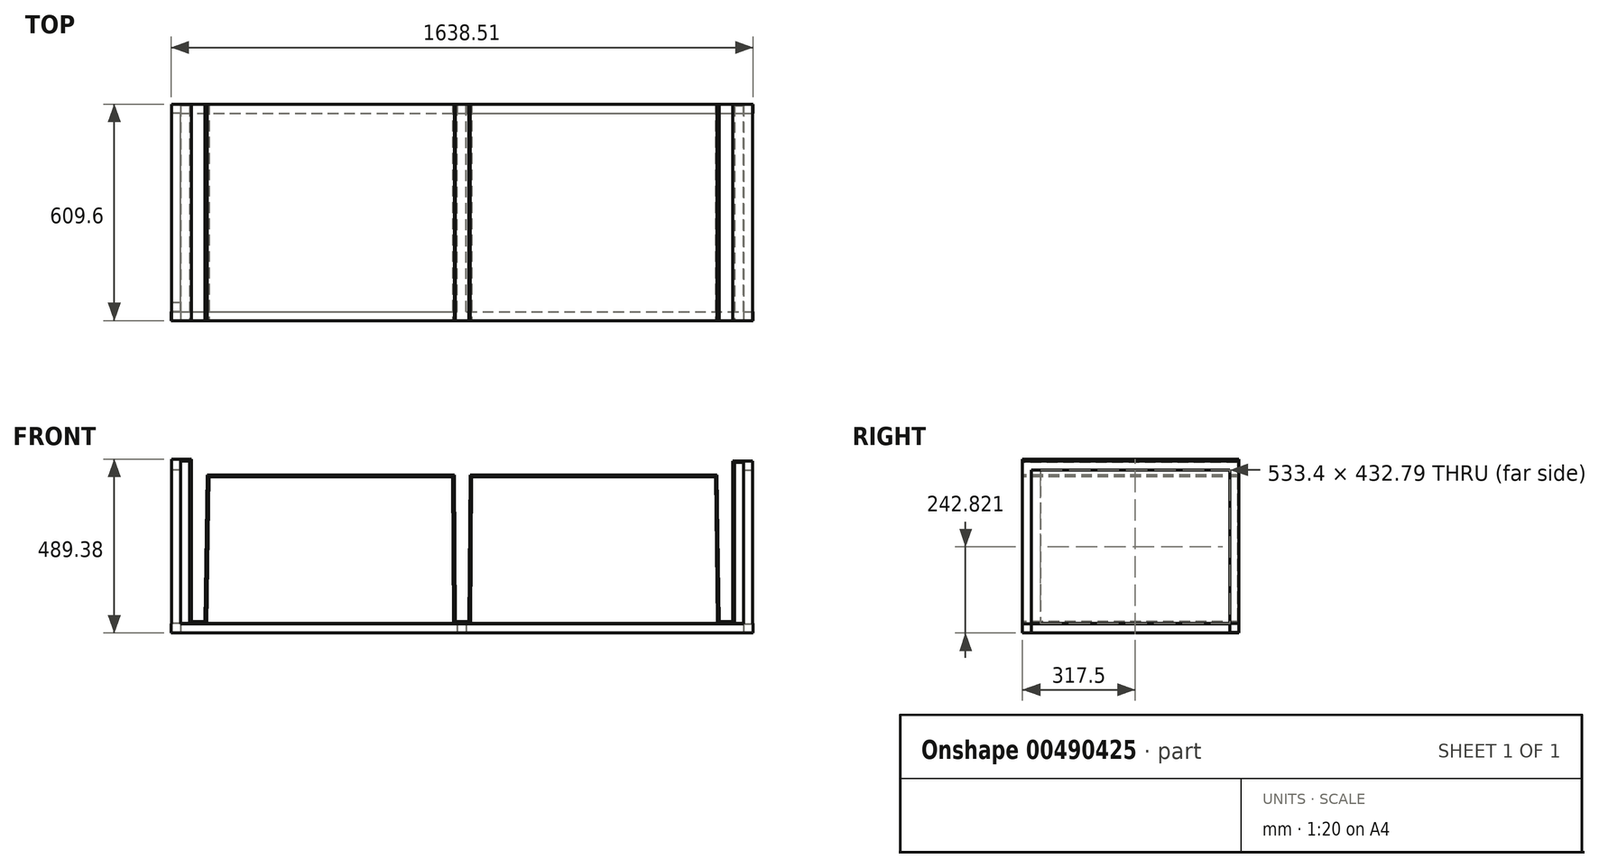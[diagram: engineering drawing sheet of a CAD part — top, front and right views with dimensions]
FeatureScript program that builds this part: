
annotation { "Feature Type Name" : "Feature", "Feature Type Description" : "" }
export const myFeature = defineFeature(function(context is Context, id is Id, definition is map)
    precondition{}
    {
        {
            var Q0;
            Q0=qCreatedBy(makeId("Front.planeOp"),FACE);
            var sketch = newSketch(context, id + "F0", { "sketchPlane" : qUnion([Q0])});
            skLineSegment(sketch, "E0", {"start": v(-453.27, -261.56) * mm, "end": v(-453.27, 195.64) * mm});
            skLineSegment(sketch, "E1", {"start": v(-453.27, -261.56) * mm, "end": v(-415.17, -261.56) * mm});
            skLineSegment(sketch, "E2", {"start": v(1070.73, 190.88) * mm, "end": v(1070.73, -261.56) * mm});
            skPoint(sketch, "E2.endSnap0", {"position": v(-434.22, -261.56) * mm});
            skLineSegment(sketch, "E3", {"start": v(-408.82, 151.19) * mm, "end": v(-415.17, -261.56) * mm});
            skLineSegment(sketch, "E4", {"start": v(1070.73, -261.56) * mm, "end": v(1032.63, -261.56) * mm});
            skLineSegment(sketch, "E5", {"start": v(1026.28, 151.19) * mm, "end": v(1032.63, -261.56) * mm});
            skLineSegment(sketch, "E6", {"start": v(-408.82, 151.19) * mm, "end": v(286.5, 151.19) * mm});
            skLineSegment(sketch, "E7", {"start": v(1026.28, 151.19) * mm, "end": v(330.96, 151.19) * mm});
            skLineSegment(sketch, "E8", {"start": v(327.78, -261.56) * mm, "end": v(330.96, 151.19) * mm});
            skLineSegment(sketch, "E9", {"start": v(327.78, -261.56) * mm, "end": v(289.68, -261.56) * mm});
            skLineSegment(sketch, "E10", {"start": v(289.68, -261.56) * mm, "end": v(286.5, 151.19) * mm});
            skLineSegment(sketch, "E11", {"start": v(-453.27, 195.64) * mm, "end": v(-458.03, 195.64) * mm});
            skLineSegment(sketch, "E12", {"start": v(-458.03, 195.64) * mm, "end": v(-458.03, -261.56) * mm});
            skLineSegment(sketch, "E13", {"start": v(-458.03, -261.56) * mm, "end": v(-453.27, -261.56) * mm});
            skLineSegment(sketch, "E14", {"start": v(-458.03, -261.56) * mm, "end": v(-458.03, -266.32) * mm});
            skLineSegment(sketch, "E15", {"start": v(-458.03, -266.32) * mm, "end": v(-415.17, -266.98) * mm});
            skLineSegment(sketch, "E16", {"start": v(-415.17, -266.98) * mm, "end": v(-415.17, -261.56) * mm});
            skLineSegment(sketch, "E17", {"start": v(-415.17, -266.98) * mm, "end": v(-410.4, -266.98) * mm});
            skLineSegment(sketch, "E18", {"start": v(-410.4, -266.98) * mm, "end": v(-403.97, 151.19) * mm});
            skLineSegment(sketch, "E19", {"start": v(-408.82, 151.19) * mm, "end": v(-408.82, 146.43) * mm});
            skLineSegment(sketch, "E20", {"start": v(-408.82, 146.43) * mm, "end": v(286.54, 146.43) * mm});
            skLineSegment(sketch, "E21", {"start": v(289.68, -261.56) * mm, "end": v(284.92, -261.56) * mm});
            skLineSegment(sketch, "E22", {"start": v(284.92, -261.56) * mm, "end": v(281.78, 146.43) * mm});
            skLineSegment(sketch, "E23", {"start": v(284.92, -261.56) * mm, "end": v(284.92, -266.32) * mm});
            skLineSegment(sketch, "E24", {"start": v(284.92, -266.32) * mm, "end": v(327.78, -266.32) * mm});
            skLineSegment(sketch, "E25", {"start": v(327.78, -266.32) * mm, "end": v(327.78, -261.56) * mm});
            skLineSegment(sketch, "E26", {"start": v(327.78, -266.32) * mm, "end": v(332.55, -266.36) * mm});
            skLineSegment(sketch, "E27", {"start": v(332.55, -266.36) * mm, "end": v(335.76, 151.19) * mm});
            skLineSegment(sketch, "E28", {"start": v(330.96, 151.19) * mm, "end": v(330.96, 146.43) * mm});
            skLineSegment(sketch, "E29", {"start": v(330.96, 146.43) * mm, "end": v(1026.36, 146.43) * mm});
            skLineSegment(sketch, "E30", {"start": v(1026.28, 151.19) * mm, "end": v(1021.52, 151.19) * mm});
            skLineSegment(sketch, "E31", {"start": v(1021.52, 151.19) * mm, "end": v(1027.87, -261.56) * mm});
            skLineSegment(sketch, "E32", {"start": v(1027.87, -261.56) * mm, "end": v(1032.63, -261.56) * mm});
            skLineSegment(sketch, "E33", {"start": v(1027.87, -261.56) * mm, "end": v(1027.87, -266.32) * mm});
            skLineSegment(sketch, "E34", {"start": v(1027.87, -266.32) * mm, "end": v(1070.73, -266.32) * mm});
            skLineSegment(sketch, "E35", {"start": v(1070.73, -266.32) * mm, "end": v(1070.73, -261.56) * mm});
            skLineSegment(sketch, "E36", {"start": v(1070.73, -266.32) * mm, "end": v(1075.5, -266.32) * mm});
            skLineSegment(sketch, "E37", {"start": v(1075.5, -266.32) * mm, "end": v(1075.5, 190.88) * mm});
            skLineSegment(sketch, "E38", {"start": v(1075.5, 190.88) * mm, "end": v(1070.73, 190.88) * mm});
            skSolve(sketch);
        }
        {
            var Q0;
            Q0 = qSketchRegion(id + "F0", true);
            extrude(context, id + "F1", {"entities" : qUnion([Q0]), "depth" : -609.6 * mm});
        }
        {
            var Q0;
            Q0=makeQuery(id+"F1.opExtrude","CAP_FACE",FACE,{"disambiguationData":[OSD([sQuery(id+"F0.wireOp",EDGE,"E0"),sQuery(id+"F0.wireOp",EDGE,"E1"),sQuery(id+"F0.wireOp",EDGE,"E2"),sQuery(id+"F0.wireOp",EDGE,"E3"),sQuery(id+"F0.wireOp",EDGE,"E4"),sQuery(id+"F0.wireOp",EDGE,"E5"),sQuery(id+"F0.wireOp",EDGE,"E6"),sQuery(id+"F0.wireOp",EDGE,"E7"),sQuery(id+"F0.wireOp",EDGE,"E8"),sQuery(id+"F0.wireOp",EDGE,"E9"),sQuery(id+"F0.wireOp",EDGE,"E10"),sQuery(id+"F0.wireOp",EDGE,"E11"),sQuery(id+"F0.wireOp",EDGE,"E12"),sQuery(id+"F0.wireOp",EDGE,"E14"),sQuery(id+"F0.wireOp",EDGE,"E15"),sQuery(id+"F0.wireOp",EDGE,"E17"),sQuery(id+"F0.wireOp",EDGE,"E18"),sQuery(id+"F0.wireOp",EDGE,"E20"),sQuery(id+"F0.wireOp",EDGE,"E22"),sQuery(id+"F0.wireOp",EDGE,"E23"),sQuery(id+"F0.wireOp",EDGE,"E24"),sQuery(id+"F0.wireOp",EDGE,"E26"),sQuery(id+"F0.wireOp",EDGE,"E27"),sQuery(id+"F0.wireOp",EDGE,"E29"),sQuery(id+"F0.wireOp",EDGE,"E30"),sQuery(id+"F0.wireOp",EDGE,"E31"),sQuery(id+"F0.wireOp",EDGE,"E33"),sQuery(id+"F0.wireOp",EDGE,"E34"),sQuery(id+"F0.wireOp",EDGE,"E36"),sQuery(id+"F0.wireOp",EDGE,"E37"),sQuery(id+"F0.wireOp",EDGE,"E38")])],"isStart":true});
            var sketch = newSketch(context, id + "F2", { "sketchPlane" : qUnion([Q0])});
            skLineSegment(sketch, "E39.bottom", {"start": v(-458.03, 195.64) * mm, "end": v(-508.83, 195.64) * mm});
            skLineSegment(sketch, "E39.top", {"start": v(-458.03, 190.88) * mm, "end": v(-508.83, 190.88) * mm});
            skLineSegment(sketch, "E39.left", {"start": v(-458.03, 195.64) * mm, "end": v(-458.03, 190.88) * mm});
            skLineSegment(sketch, "E39.right", {"start": v(-508.83, 195.64) * mm, "end": v(-508.83, 190.88) * mm});
            skLineSegment(sketch, "E40.bottom", {"start": v(1075.5, 190.88) * mm, "end": v(1126.3, 190.88) * mm});
            skLineSegment(sketch, "E40.top", {"start": v(1075.5, 186.11) * mm, "end": v(1126.3, 186.11) * mm});
            skLineSegment(sketch, "E40.left", {"start": v(1075.5, 190.88) * mm, "end": v(1075.5, 186.11) * mm});
            skLineSegment(sketch, "E40.right", {"start": v(1126.3, 190.88) * mm, "end": v(1126.3, 186.11) * mm});
            skSolve(sketch);
        }
        {
            var Q0;
            Q0=makeQuery(id+"F2.imprint","IMPRINT",FACE,{"disambiguationData":[TD([[makeQuery(id+"F2.imprint","IMPRINT",EDGE,{"derivedFrom":sQuery(id+"F2.wireOp",EDGE,"E39.bottom")}),1.0]])]});
            extrude(context, id + "F3", {"entities" : qUnion([Q0]), "operationType" : NewBodyOperationType.ADD, "depth" : -609.6 * mm});
        }
        {
            var Q0;
            Q0 = qSketchRegion(id + "F2", true);
            extrude(context, id + "F4", {"entities" : qUnion([Q0]), "operationType" : NewBodyOperationType.ADD, "depth" : -609.6 * mm});
        }
        {
            var Q0;
            Q0=makeQuery(id+"F4.boolean.opBoolean","MERGE",FACE,{"derivedFrom":[makeQuery(id+"F3.boolean.opBoolean","MERGE",FACE,{"derivedFrom":[makeQuery(id+"F1.opExtrude","CAP_FACE",FACE,{"disambiguationData":[OSD([sQuery(id+"F0.wireOp",EDGE,"E0"),sQuery(id+"F0.wireOp",EDGE,"E1"),sQuery(id+"F0.wireOp",EDGE,"E2"),sQuery(id+"F0.wireOp",EDGE,"E3"),sQuery(id+"F0.wireOp",EDGE,"E4"),sQuery(id+"F0.wireOp",EDGE,"E5"),sQuery(id+"F0.wireOp",EDGE,"E6"),sQuery(id+"F0.wireOp",EDGE,"E7"),sQuery(id+"F0.wireOp",EDGE,"E8"),sQuery(id+"F0.wireOp",EDGE,"E9"),sQuery(id+"F0.wireOp",EDGE,"E10"),sQuery(id+"F0.wireOp",EDGE,"E11"),sQuery(id+"F0.wireOp",EDGE,"E12"),sQuery(id+"F0.wireOp",EDGE,"E14"),sQuery(id+"F0.wireOp",EDGE,"E15"),sQuery(id+"F0.wireOp",EDGE,"E17"),sQuery(id+"F0.wireOp",EDGE,"E18"),sQuery(id+"F0.wireOp",EDGE,"E20"),sQuery(id+"F0.wireOp",EDGE,"E22"),sQuery(id+"F0.wireOp",EDGE,"E23"),sQuery(id+"F0.wireOp",EDGE,"E24"),sQuery(id+"F0.wireOp",EDGE,"E26"),sQuery(id+"F0.wireOp",EDGE,"E27"),sQuery(id+"F0.wireOp",EDGE,"E29"),sQuery(id+"F0.wireOp",EDGE,"E30"),sQuery(id+"F0.wireOp",EDGE,"E31"),sQuery(id+"F0.wireOp",EDGE,"E33"),sQuery(id+"F0.wireOp",EDGE,"E34"),sQuery(id+"F0.wireOp",EDGE,"E36"),sQuery(id+"F0.wireOp",EDGE,"E37"),sQuery(id+"F0.wireOp",EDGE,"E38")])],"isStart":true}),makeQuery(id+"F3.opExtrude","CAP_FACE",FACE,{"disambiguationData":[OSD([sQuery(id+"F2.wireOp",EDGE,"E39.bottom"),sQuery(id+"F2.wireOp",EDGE,"E39.top"),sQuery(id+"F2.wireOp",EDGE,"E39.left"),sQuery(id+"F2.wireOp",EDGE,"E39.right")])],"isStart":true})]}),makeQuery(id+"F4.opExtrude","CAP_FACE",FACE,{"disambiguationData":[OSD([sQuery(id+"F2.wireOp",EDGE,"E40.bottom"),sQuery(id+"F2.wireOp",EDGE,"E40.top"),sQuery(id+"F2.wireOp",EDGE,"E40.left"),sQuery(id+"F2.wireOp",EDGE,"E40.right")])],"isStart":true})]});
            var sketch = newSketch(context, id + "F5", { "sketchPlane" : qUnion([Q0])});
            skLineSegment(sketch, "E41.bottom", {"start": v(-508.83, 190.88) * mm, "end": v(-483.43, 190.88) * mm});
            skLineSegment(sketch, "E41.top", {"start": v(-508.83, -271.09) * mm, "end": v(-483.43, -271.09) * mm});
            skLineSegment(sketch, "E41.left", {"start": v(-508.83, 190.88) * mm, "end": v(-508.83, -271.09) * mm});
            skLineSegment(sketch, "E41.right", {"start": v(-483.43, 190.88) * mm, "end": v(-483.43, -271.09) * mm});
            skLineSegment(sketch, "E42.bottom", {"start": v(1126.3, 186.11) * mm, "end": v(1100.9, 186.11) * mm});
            skLineSegment(sketch, "E42.top", {"start": v(1126.3, -275.85) * mm, "end": v(1100.9, -275.85) * mm});
            skLineSegment(sketch, "E42.left", {"start": v(1126.3, 186.11) * mm, "end": v(1126.3, -275.85) * mm});
            skLineSegment(sketch, "E42.right", {"start": v(1100.9, 186.11) * mm, "end": v(1100.9, -275.85) * mm});
            skSolve(sketch);
        }
        {
            var Q0;
            Q0 = qSketchRegion(id + "F5", true);
            extrude(context, id + "F6", {"entities" : qUnion([Q0]), "operationType" : NewBodyOperationType.ADD, "depth" : -25.4 * mm});
        }
        {
            var Q0;
            Q0=makeQuery(id+"F6.boolean.opBoolean","MERGE",FACE,{"derivedFrom":[makeQuery(id+"F4.boolean.opBoolean","MERGE",FACE,{"derivedFrom":[makeQuery(id+"F3.boolean.opBoolean","MERGE",FACE,{"derivedFrom":[makeQuery(id+"F1.opExtrude","CAP_FACE",FACE,{"disambiguationData":[OSD([sQuery(id+"F0.wireOp",EDGE,"E0"),sQuery(id+"F0.wireOp",EDGE,"E1"),sQuery(id+"F0.wireOp",EDGE,"E2"),sQuery(id+"F0.wireOp",EDGE,"E3"),sQuery(id+"F0.wireOp",EDGE,"E4"),sQuery(id+"F0.wireOp",EDGE,"E5"),sQuery(id+"F0.wireOp",EDGE,"E6"),sQuery(id+"F0.wireOp",EDGE,"E7"),sQuery(id+"F0.wireOp",EDGE,"E8"),sQuery(id+"F0.wireOp",EDGE,"E9"),sQuery(id+"F0.wireOp",EDGE,"E10"),sQuery(id+"F0.wireOp",EDGE,"E11"),sQuery(id+"F0.wireOp",EDGE,"E12"),sQuery(id+"F0.wireOp",EDGE,"E14"),sQuery(id+"F0.wireOp",EDGE,"E15"),sQuery(id+"F0.wireOp",EDGE,"E17"),sQuery(id+"F0.wireOp",EDGE,"E18"),sQuery(id+"F0.wireOp",EDGE,"E20"),sQuery(id+"F0.wireOp",EDGE,"E22"),sQuery(id+"F0.wireOp",EDGE,"E23"),sQuery(id+"F0.wireOp",EDGE,"E24"),sQuery(id+"F0.wireOp",EDGE,"E26"),sQuery(id+"F0.wireOp",EDGE,"E27"),sQuery(id+"F0.wireOp",EDGE,"E29"),sQuery(id+"F0.wireOp",EDGE,"E30"),sQuery(id+"F0.wireOp",EDGE,"E31"),sQuery(id+"F0.wireOp",EDGE,"E33"),sQuery(id+"F0.wireOp",EDGE,"E34"),sQuery(id+"F0.wireOp",EDGE,"E36"),sQuery(id+"F0.wireOp",EDGE,"E37"),sQuery(id+"F0.wireOp",EDGE,"E38")])],"isStart":true}),makeQuery(id+"F3.opExtrude","CAP_FACE",FACE,{"disambiguationData":[OSD([sQuery(id+"F2.wireOp",EDGE,"E39.bottom"),sQuery(id+"F2.wireOp",EDGE,"E39.top"),sQuery(id+"F2.wireOp",EDGE,"E39.left"),sQuery(id+"F2.wireOp",EDGE,"E39.right")])],"isStart":true})]}),makeQuery(id+"F4.opExtrude","CAP_FACE",FACE,{"disambiguationData":[OSD([sQuery(id+"F2.wireOp",EDGE,"E40.bottom"),sQuery(id+"F2.wireOp",EDGE,"E40.top"),sQuery(id+"F2.wireOp",EDGE,"E40.left"),sQuery(id+"F2.wireOp",EDGE,"E40.right")])],"isStart":true})]}),makeQuery(id+"F6.opExtrude","CAP_FACE",FACE,{"disambiguationData":[OSD([sQuery(id+"F5.wireOp",EDGE,"PXd4t3fK-VJNK-RpV8-3AYd-AQfVrzeM2m9b.bottom"),sQuery(id+"F5.wireOp",EDGE,"PXd4t3fK-VJNK-RpV8-3AYd-AQfVrzeM2m9b.top"),sQuery(id+"F5.wireOp",EDGE,"PXd4t3fK-VJNK-RpV8-3AYd-AQfVrzeM2m9b.left"),sQuery(id+"F5.wireOp",EDGE,"PXd4t3fK-VJNK-RpV8-3AYd-AQfVrzeM2m9b.right")])],"isStart":true}),makeQuery(id+"F6.opExtrude","CAP_FACE",FACE,{"disambiguationData":[OSD([sQuery(id+"F5.wireOp",EDGE,"UQCXd49x-7FcS-RsmS-loZU-28u0bhkUhXdd.bottom"),sQuery(id+"F5.wireOp",EDGE,"UQCXd49x-7FcS-RsmS-loZU-28u0bhkUhXdd.top"),sQuery(id+"F5.wireOp",EDGE,"UQCXd49x-7FcS-RsmS-loZU-28u0bhkUhXdd.left"),sQuery(id+"F5.wireOp",EDGE,"UQCXd49x-7FcS-RsmS-loZU-28u0bhkUhXdd.right")])],"isStart":true})]});
            var sketch = newSketch(context, id + "F7", { "sketchPlane" : qUnion([Q0])});
            skSolve(sketch);
        }
        {
            var Q0;
            Q0 = qSketchRegion(id + "F5", true);
            extrude(context, id + "F8", {"entities" : qUnion([Q0]), "operationType" : NewBodyOperationType.ADD, "depth" : -25.4 * mm});
        }
        {
            var Q0;
            Q0=makeQuery(id+"F7.imprint","IMPRINT",FACE,{"disambiguationData":[TD([[makeQuery(id+"F7.imprint","IMPRINT",EDGE,{"derivedFrom":makeQuery(id+"F1.opExtrude","CAP_EDGE",EDGE,{"disambiguationData":[OSD([sQuery(id+"F0.wireOp",EDGE,"E0")])],"isStart":true})}),1.0]])]});
            var sketch = newSketch(context, id + "F9", { "sketchPlane" : qUnion([Q0])});
            skLineSegment(sketch, "E43.bottom", {"start": v(-510.8, -268.34) * mm, "end": v(1127.1, -268.34) * mm});
            skLineSegment(sketch, "E43.top", {"start": v(-510.8, -293.74) * mm, "end": v(1127.1, -293.74) * mm});
            skLineSegment(sketch, "E43.left", {"start": v(-510.8, -268.34) * mm, "end": v(-510.8, -293.74) * mm});
            skLineSegment(sketch, "E43.right", {"start": v(1127.1, -268.34) * mm, "end": v(1127.1, -293.74) * mm});
            skSolve(sketch);
        }
        {
            var Q0;
            Q0 = qSketchRegion(id + "F9", true);
            extrude(context, id + "F10", {"entities" : qUnion([Q0]), "operationType" : NewBodyOperationType.ADD, "depth" : -25.4 * mm});
        }
        {
            var Q0;
            Q0=makeQuery(id+"F6.boolean.opBoolean","MERGE",FACE,{"derivedFrom":[makeQuery(id+"F4.opExtrude","SWEPT_FACE",FACE,{"disambiguationData":[OSD([sQuery(id+"F2.wireOp",EDGE,"E40.right")])]}),makeQuery(id+"F6.opExtrude","SWEPT_FACE",FACE,{"disambiguationData":[OSD([sQuery(id+"F5.wireOp",EDGE,"E42.left")])]})]});
            var sketch = newSketch(context, id + "F11", { "sketchPlane" : qUnion([Q0])});
            skLineSegment(sketch, "E44.bottom", {"start": v(0, 190.88) * mm, "end": v(609.6, 190.88) * mm});
            skLineSegment(sketch, "E44.top", {"start": v(0, 165.48) * mm, "end": v(609.6, 165.48) * mm});
            skLineSegment(sketch, "E44.left", {"start": v(0, 190.88) * mm, "end": v(0, 165.48) * mm});
            skLineSegment(sketch, "E44.right", {"start": v(609.6, 190.88) * mm, "end": v(609.6, 165.48) * mm});
            skLineSegment(sketch, "E45.bottom", {"start": v(609.6, 165.48) * mm, "end": v(584.2, 165.48) * mm});
            skLineSegment(sketch, "E46.bottom", {"start": v(25.4, -268.34) * mm, "end": v(609.6, -268.34) * mm});
            skLineSegment(sketch, "E46.top", {"start": v(25.4, -293.74) * mm, "end": v(609.6, -293.74) * mm});
            skLineSegment(sketch, "E46.left", {"start": v(25.4, -268.34) * mm, "end": v(25.4, -293.74) * mm});
            skLineSegment(sketch, "E46.right", {"start": v(609.6, -268.34) * mm, "end": v(609.6, -293.74) * mm});
            skLineSegment(sketch, "E47.top", {"start": v(609.6, -268.34) * mm, "end": v(584.2, -268.34) * mm});
            skLineSegment(sketch, "E47.left", {"start": v(609.6, 165.48) * mm, "end": v(609.6, -268.34) * mm});
            skLineSegment(sketch, "E47.right", {"start": v(584.2, 165.48) * mm, "end": v(584.2, -268.34) * mm});
            skSolve(sketch);
        }
        {
            var Q0;
            Q0 = qSketchRegion(id + "F11", true);
            extrude(context, id + "F12", {"entities" : qUnion([Q0]), "operationType" : NewBodyOperationType.ADD, "depth" : -25.4 * mm});
        }
        {
            var Q0;
            Q0 = qSketchRegion(id + "F11", true);
            extrude(context, id + "F13", {"entities" : qUnion([Q0]), "operationType" : NewBodyOperationType.ADD, "depth" : -25.4 * mm});
        }
        {
            var Q0;
            Q0=makeQuery(id+"F6.boolean.opBoolean","MERGE",FACE,{"derivedFrom":[makeQuery(id+"F3.opExtrude","SWEPT_FACE",FACE,{"disambiguationData":[OSD([sQuery(id+"F2.wireOp",EDGE,"E39.right")])]}),makeQuery(id+"F6.opExtrude","SWEPT_FACE",FACE,{"disambiguationData":[OSD([sQuery(id+"F5.wireOp",EDGE,"E41.left")])]})]});
            var sketch = newSketch(context, id + "F14", { "sketchPlane" : qUnion([Q0])});
            skLineSegment(sketch, "E48.bottom", {"start": v(-25.4, 190.88) * mm, "end": v(-609.6, 190.88) * mm});
            skLineSegment(sketch, "E48.top", {"start": v(-25.4, 165.48) * mm, "end": v(-609.6, 165.48) * mm});
            skLineSegment(sketch, "E48.left", {"start": v(-25.4, 190.88) * mm, "end": v(-25.4, 165.48) * mm});
            skLineSegment(sketch, "E48.right", {"start": v(-609.6, 190.88) * mm, "end": v(-609.6, 165.48) * mm});
            skLineSegment(sketch, "E49.bottom", {"start": v(-25.4, 165.48) * mm, "end": v(-50.8, 165.48) * mm});
            skLineSegment(sketch, "E49.top", {"start": v(-25.4, -267.32) * mm, "end": v(-50.8, -267.32) * mm});
            skLineSegment(sketch, "E49.left", {"start": v(-25.4, 165.48) * mm, "end": v(-25.4, -267.32) * mm});
            skLineSegment(sketch, "E49.right", {"start": v(-50.8, 165.48) * mm, "end": v(-50.8, -267.32) * mm});
            skLineSegment(sketch, "E50.bottom", {"start": v(-25.4, -267.32) * mm, "end": v(-609.6, -267.32) * mm});
            skLineSegment(sketch, "E50.top", {"start": v(-25.4, -292.72) * mm, "end": v(-609.6, -292.72) * mm});
            skLineSegment(sketch, "E50.left", {"start": v(-25.4, -267.32) * mm, "end": v(-25.4, -292.72) * mm});
            skLineSegment(sketch, "E50.right", {"start": v(-609.6, -267.32) * mm, "end": v(-609.6, -292.72) * mm});
            skLineSegment(sketch, "E51.bottom", {"start": v(-609.6, 165.48) * mm, "end": v(-584.2, 165.48) * mm});
            skLineSegment(sketch, "E51.top", {"start": v(-609.6, -267.32) * mm, "end": v(-584.2, -267.32) * mm});
            skLineSegment(sketch, "E51.left", {"start": v(-609.6, 165.48) * mm, "end": v(-609.6, -267.32) * mm});
            skLineSegment(sketch, "E51.right", {"start": v(-584.2, 165.48) * mm, "end": v(-584.2, -267.32) * mm});
            skSolve(sketch);
        }
        {
            var Q0;
            Q0 = qSketchRegion(id + "F14", true);
            extrude(context, id + "F15", {"entities" : qUnion([Q0]), "operationType" : NewBodyOperationType.ADD, "depth" : -25.4 * mm});
        }
        {
            var Q0;
            Q0=makeQuery(id+"F15.opExtrude","SWEPT_FACE",FACE,{"disambiguationData":[OSD([sQuery(id+"F14.wireOp",EDGE,"E50.top")])]});
            var sketch = newSketch(context, id + "F16", { "sketchPlane" : qUnion([Q0])});
            skLineSegment(sketch, "E52.bottom", {"start": v(-508.83, -609.6) * mm, "end": v(1127.72, -609.6) * mm});
            skLineSegment(sketch, "E52.top", {"start": v(-508.83, -584.2) * mm, "end": v(1127.72, -584.2) * mm});
            skLineSegment(sketch, "E52.left", {"start": v(-508.83, -609.6) * mm, "end": v(-508.83, -584.2) * mm});
            skLineSegment(sketch, "E52.right", {"start": v(1127.72, -609.6) * mm, "end": v(1127.72, -584.2) * mm});
            skSolve(sketch);
        }
        {
            var Q0;
            Q0 = qSketchRegion(id + "F16", true);
            extrude(context, id + "F17", {"entities" : qUnion([Q0]), "operationType" : NewBodyOperationType.ADD, "depth" : -25.4 * mm});
        }
        {
            var Q0;
            Q0=makeQuery(id+"F12.boolean.opBoolean","MERGE",FACE,{"derivedFrom":[makeQuery(id+"F10.opExtrude","SWEPT_FACE",FACE,{"disambiguationData":[OSD([sQuery(id+"F9.wireOp",EDGE,"E43.top")])]}),makeQuery(id+"F12.opExtrude","SWEPT_FACE",FACE,{"disambiguationData":[OSD([sQuery(id+"F11.wireOp",EDGE,"E46.top")])]})]});
            var sketch = newSketch(context, id + "F18", { "sketchPlane" : qUnion([Q0])});
            skPoint(sketch, "E53.firstSnap0", {"position": v(295.05, -25.4) * mm});
            skLineSegment(sketch, "E53.bottom", {"start": v(295.05, 0) * mm, "end": v(320.45, 0) * mm});
            skLineSegment(sketch, "E53.top", {"start": v(295.05, -609.6) * mm, "end": v(320.45, -609.6) * mm});
            skLineSegment(sketch, "E53.left", {"start": v(295.05, 0) * mm, "end": v(295.05, -609.6) * mm});
            skLineSegment(sketch, "E53.right", {"start": v(320.45, 0) * mm, "end": v(320.45, -609.6) * mm});
            skSolve(sketch);
        }
        {
            var Q0;
            Q0 = qSketchRegion(id + "F18", true);
            extrude(context, id + "F19", {"entities" : qUnion([Q0]), "operationType" : NewBodyOperationType.ADD, "depth" : -25.4 * mm});
        }
        {
            var Q0;
            Q0=makeQuery(id+"F19.boolean.opBoolean","MERGE",FACE,{"derivedFrom":[makeQuery(id+"F17.boolean.opBoolean","MERGE",FACE,{"derivedFrom":[makeQuery(id+"F15.boolean.opBoolean","MERGE",FACE,{"derivedFrom":[makeQuery(id+"F12.boolean.opBoolean","MERGE",FACE,{"derivedFrom":[makeQuery(id+"F4.boolean.opBoolean","MERGE",FACE,{"derivedFrom":[makeQuery(id+"F3.boolean.opBoolean","MERGE",FACE,{"derivedFrom":[makeQuery(id+"F1.opExtrude","CAP_FACE",FACE,{"disambiguationData":[OSD([sQuery(id+"F0.wireOp",EDGE,"E0"),sQuery(id+"F0.wireOp",EDGE,"E1"),sQuery(id+"F0.wireOp",EDGE,"E2"),sQuery(id+"F0.wireOp",EDGE,"E3"),sQuery(id+"F0.wireOp",EDGE,"E4"),sQuery(id+"F0.wireOp",EDGE,"E5"),sQuery(id+"F0.wireOp",EDGE,"E6"),sQuery(id+"F0.wireOp",EDGE,"E7"),sQuery(id+"F0.wireOp",EDGE,"E8"),sQuery(id+"F0.wireOp",EDGE,"E9"),sQuery(id+"F0.wireOp",EDGE,"E10"),sQuery(id+"F0.wireOp",EDGE,"E11"),sQuery(id+"F0.wireOp",EDGE,"E12"),sQuery(id+"F0.wireOp",EDGE,"E14"),sQuery(id+"F0.wireOp",EDGE,"E15"),sQuery(id+"F0.wireOp",EDGE,"E17"),sQuery(id+"F0.wireOp",EDGE,"E18"),sQuery(id+"F0.wireOp",EDGE,"E20"),sQuery(id+"F0.wireOp",EDGE,"E22"),sQuery(id+"F0.wireOp",EDGE,"E23"),sQuery(id+"F0.wireOp",EDGE,"E24"),sQuery(id+"F0.wireOp",EDGE,"E26"),sQuery(id+"F0.wireOp",EDGE,"E27"),sQuery(id+"F0.wireOp",EDGE,"E29"),sQuery(id+"F0.wireOp",EDGE,"E30"),sQuery(id+"F0.wireOp",EDGE,"E31"),sQuery(id+"F0.wireOp",EDGE,"E33"),sQuery(id+"F0.wireOp",EDGE,"E34"),sQuery(id+"F0.wireOp",EDGE,"E36"),sQuery(id+"F0.wireOp",EDGE,"E37"),sQuery(id+"F0.wireOp",EDGE,"E38")])],"isStart":false}),makeQuery(id+"F3.opExtrude","CAP_FACE",FACE,{"disambiguationData":[OSD([sQuery(id+"F2.wireOp",EDGE,"E39.bottom"),sQuery(id+"F2.wireOp",EDGE,"E39.top"),sQuery(id+"F2.wireOp",EDGE,"E39.left"),sQuery(id+"F2.wireOp",EDGE,"E39.right")])],"isStart":false})]}),makeQuery(id+"F4.opExtrude","CAP_FACE",FACE,{"disambiguationData":[OSD([sQuery(id+"F2.wireOp",EDGE,"E40.bottom"),sQuery(id+"F2.wireOp",EDGE,"E40.top"),sQuery(id+"F2.wireOp",EDGE,"E40.left"),sQuery(id+"F2.wireOp",EDGE,"E40.right")])],"isStart":false})]}),makeQuery(id+"F12.opExtrude","SWEPT_FACE",FACE,{"disambiguationData":[OSD([sQuery(id+"F11.wireOp",EDGE,"E44.right"),sQuery(id+"F11.wireOp",EDGE,"E46.right"),sQuery(id+"F11.wireOp",EDGE,"E47.left")])]})]}),makeQuery(id+"F15.opExtrude","SWEPT_FACE",FACE,{"disambiguationData":[OSD([sQuery(id+"F14.wireOp",EDGE,"E48.right"),sQuery(id+"F14.wireOp",EDGE,"E50.right"),sQuery(id+"F14.wireOp",EDGE,"E51.left")])]})]}),makeQuery(id+"F17.opExtrude","SWEPT_FACE",FACE,{"disambiguationData":[OSD([sQuery(id+"F16.wireOp",EDGE,"E52.bottom")])]})]}),makeQuery(id+"F19.opExtrude","SWEPT_FACE",FACE,{"disambiguationData":[OSD([sQuery(id+"F18.wireOp",EDGE,"E53.top")])]})]});
            var sketch = newSketch(context, id + "F20", { "sketchPlane" : qUnion([Q0])});
            skLineSegment(sketch, "E54.bottom", {"start": v(-1075.5, 186.11) * mm, "end": v(-1126.3, 186.11) * mm});
            skLineSegment(sketch, "E54.top", {"start": v(-1075.5, -267.32) * mm, "end": v(-1126.3, -267.32) * mm});
            skLineSegment(sketch, "E54.left", {"start": v(-1075.5, 186.11) * mm, "end": v(-1075.5, -267.32) * mm});
            skLineSegment(sketch, "E54.right", {"start": v(-1126.3, 186.11) * mm, "end": v(-1126.3, -267.32) * mm});
            skSolve(sketch);
        }
        {
            var Q0;
            Q0 = qSketchRegion(id + "F20", true);
            extrude(context, id + "F21", {"entities" : qUnion([Q0]), "operationType" : NewBodyOperationType.ADD, "depth" : -4.76 * mm});
        }
        {
            var Q0;
            Q0=makeQuery(id+"F21.boolean.opBoolean","MERGE",FACE,{"derivedFrom":[makeQuery(id+"F19.boolean.opBoolean","MERGE",FACE,{"derivedFrom":[makeQuery(id+"F17.boolean.opBoolean","MERGE",FACE,{"derivedFrom":[makeQuery(id+"F15.boolean.opBoolean","MERGE",FACE,{"derivedFrom":[makeQuery(id+"F12.boolean.opBoolean","MERGE",FACE,{"derivedFrom":[makeQuery(id+"F4.boolean.opBoolean","MERGE",FACE,{"derivedFrom":[makeQuery(id+"F3.boolean.opBoolean","MERGE",FACE,{"derivedFrom":[makeQuery(id+"F1.opExtrude","CAP_FACE",FACE,{"disambiguationData":[OSD([sQuery(id+"F0.wireOp",EDGE,"E0"),sQuery(id+"F0.wireOp",EDGE,"E1"),sQuery(id+"F0.wireOp",EDGE,"E2"),sQuery(id+"F0.wireOp",EDGE,"E3"),sQuery(id+"F0.wireOp",EDGE,"E4"),sQuery(id+"F0.wireOp",EDGE,"E5"),sQuery(id+"F0.wireOp",EDGE,"E6"),sQuery(id+"F0.wireOp",EDGE,"E7"),sQuery(id+"F0.wireOp",EDGE,"E8"),sQuery(id+"F0.wireOp",EDGE,"E9"),sQuery(id+"F0.wireOp",EDGE,"E10"),sQuery(id+"F0.wireOp",EDGE,"E11"),sQuery(id+"F0.wireOp",EDGE,"E12"),sQuery(id+"F0.wireOp",EDGE,"E14"),sQuery(id+"F0.wireOp",EDGE,"E15"),sQuery(id+"F0.wireOp",EDGE,"E17"),sQuery(id+"F0.wireOp",EDGE,"E18"),sQuery(id+"F0.wireOp",EDGE,"E20"),sQuery(id+"F0.wireOp",EDGE,"E22"),sQuery(id+"F0.wireOp",EDGE,"E23"),sQuery(id+"F0.wireOp",EDGE,"E24"),sQuery(id+"F0.wireOp",EDGE,"E26"),sQuery(id+"F0.wireOp",EDGE,"E27"),sQuery(id+"F0.wireOp",EDGE,"E29"),sQuery(id+"F0.wireOp",EDGE,"E30"),sQuery(id+"F0.wireOp",EDGE,"E31"),sQuery(id+"F0.wireOp",EDGE,"E33"),sQuery(id+"F0.wireOp",EDGE,"E34"),sQuery(id+"F0.wireOp",EDGE,"E36"),sQuery(id+"F0.wireOp",EDGE,"E37"),sQuery(id+"F0.wireOp",EDGE,"E38")])],"isStart":false}),makeQuery(id+"F3.opExtrude","CAP_FACE",FACE,{"disambiguationData":[OSD([sQuery(id+"F2.wireOp",EDGE,"E39.bottom"),sQuery(id+"F2.wireOp",EDGE,"E39.top"),sQuery(id+"F2.wireOp",EDGE,"E39.left"),sQuery(id+"F2.wireOp",EDGE,"E39.right")])],"isStart":false})]}),makeQuery(id+"F4.opExtrude","CAP_FACE",FACE,{"disambiguationData":[OSD([sQuery(id+"F2.wireOp",EDGE,"E40.bottom"),sQuery(id+"F2.wireOp",EDGE,"E40.top"),sQuery(id+"F2.wireOp",EDGE,"E40.left"),sQuery(id+"F2.wireOp",EDGE,"E40.right")])],"isStart":false})]}),makeQuery(id+"F12.opExtrude","SWEPT_FACE",FACE,{"disambiguationData":[OSD([sQuery(id+"F11.wireOp",EDGE,"E44.right"),sQuery(id+"F11.wireOp",EDGE,"E46.right"),sQuery(id+"F11.wireOp",EDGE,"E47.left")])]})]}),makeQuery(id+"F15.opExtrude","SWEPT_FACE",FACE,{"disambiguationData":[OSD([sQuery(id+"F14.wireOp",EDGE,"E48.right"),sQuery(id+"F14.wireOp",EDGE,"E50.right"),sQuery(id+"F14.wireOp",EDGE,"E51.left")])]})]}),makeQuery(id+"F17.opExtrude","SWEPT_FACE",FACE,{"disambiguationData":[OSD([sQuery(id+"F16.wireOp",EDGE,"E52.bottom")])]})]}),makeQuery(id+"F19.opExtrude","SWEPT_FACE",FACE,{"disambiguationData":[OSD([sQuery(id+"F18.wireOp",EDGE,"E53.top")])]})]}),makeQuery(id+"F21.opExtrude","CAP_FACE",FACE,{"disambiguationData":[OSD([sQuery(id+"F20.wireOp",EDGE,"E54.bottom"),sQuery(id+"F20.wireOp",EDGE,"E54.top"),sQuery(id+"F20.wireOp",EDGE,"E54.left"),sQuery(id+"F20.wireOp",EDGE,"E54.right")])],"isStart":true})]});
            var sketch = newSketch(context, id + "F22", { "sketchPlane" : qUnion([Q0])});
            skLineSegment(sketch, "E55.bottom", {"start": v(483.43, 190.88) * mm, "end": v(458.03, 190.88) * mm});
            skLineSegment(sketch, "E55.top", {"start": v(483.43, -266.32) * mm, "end": v(458.03, -266.32) * mm});
            skLineSegment(sketch, "E55.left", {"start": v(483.43, 190.88) * mm, "end": v(483.43, -266.32) * mm});
            skLineSegment(sketch, "E55.right", {"start": v(458.03, 190.88) * mm, "end": v(458.03, -266.32) * mm});
            skSolve(sketch);
        }
        {
            var Q0;
            Q0 = qSketchRegion(id + "F22", true);
            extrude(context, id + "F23", {"entities" : qUnion([Q0]), "operationType" : NewBodyOperationType.ADD, "depth" : -4.76 * mm});
        }
    });
